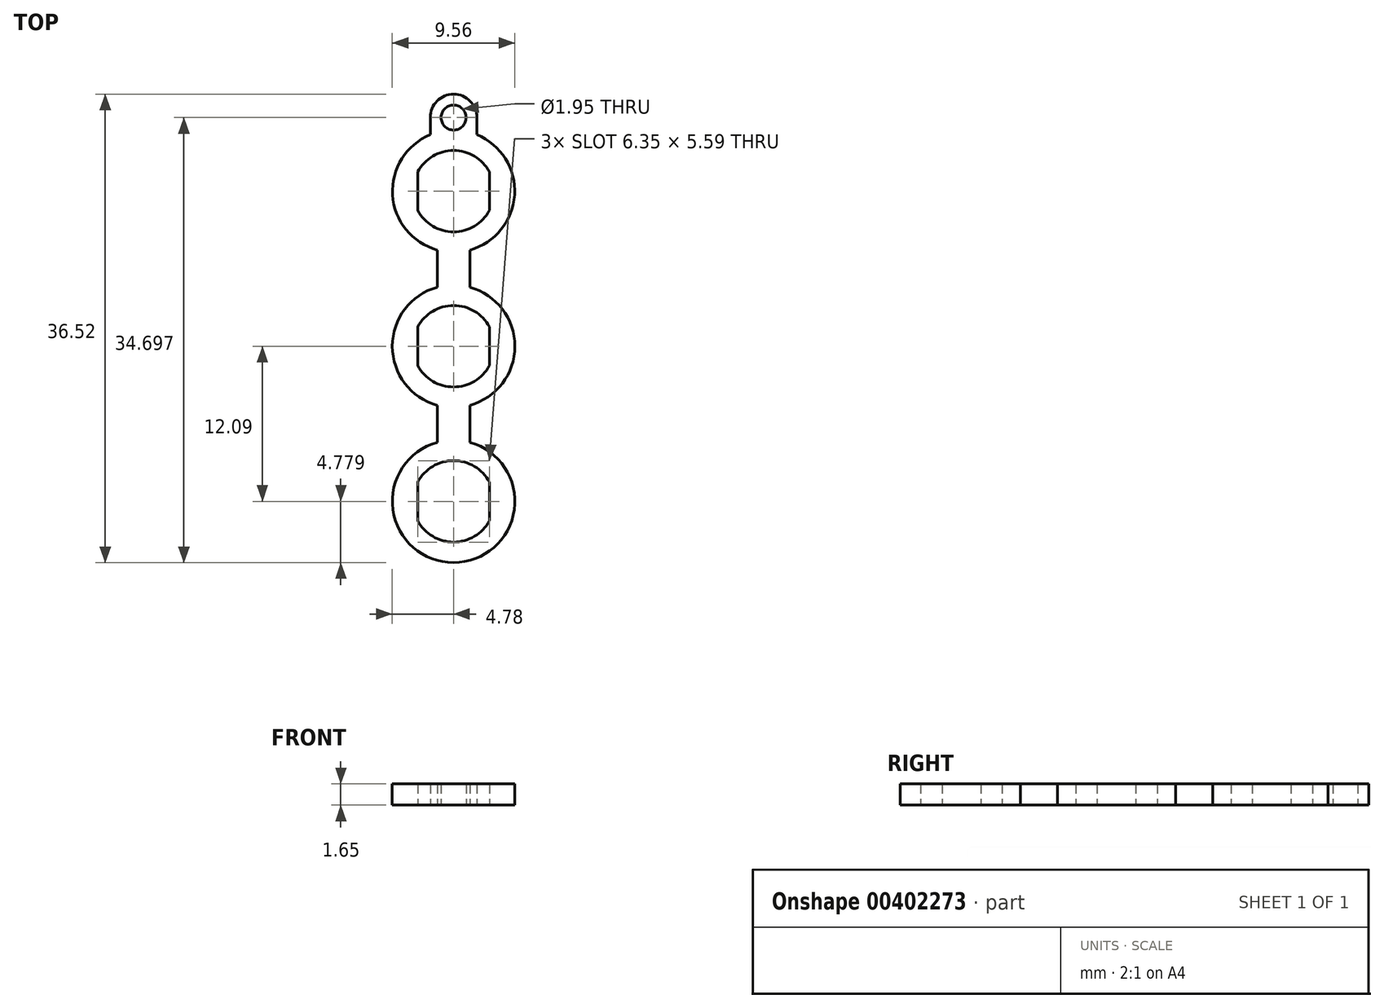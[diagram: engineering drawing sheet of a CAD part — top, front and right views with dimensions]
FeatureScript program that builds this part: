
annotation { "Feature Type Name" : "Feature", "Feature Type Description" : "" }
export const myFeature = defineFeature(function(context is Context, id is Id, definition is map)
    precondition{}
    {
        {
            var Q0;
            Q0=qCreatedBy(makeId("Top.planeOp"),FACE);
            var sketch = newSketch(context, id + "F0", { "sketchPlane" : qUnion([Q0])});
            skArc(sketch, "E0", {"start": v(1.27, -4.6) * mm, "mid": v(0, 4.76) * mm, "end": v(-1.27, -4.6) * mm});
            skArc(sketch, "E1", {"start": v(-1.27, -7.49) * mm, "mid": v(-4.78, -12.1) * mm, "end": v(-1.27, -16.7) * mm});
            skArc(sketch, "E2", {"start": v(-1.27, -19.58) * mm, "mid": v(0, -28.96) * mm, "end": v(1.27, -19.58) * mm});
            skLineSegment(sketch, "E3.0", {"start": v(-1.27, -4.6) * mm, "end": v(-1.27, -7.49) * mm});
            skLineSegment(sketch, "E4.0", {"start": v(1.27, -4.6) * mm, "end": v(1.27, -7.49) * mm});
            skLineSegment(sketch, "E5.trimOffspring", {"start": v(1.27, -16.7) * mm, "end": v(1.27, -19.58) * mm});
            skLineSegment(sketch, "E6.trimOffspring", {"start": v(-1.27, -16.7) * mm, "end": v(-1.27, -19.58) * mm});
            skArc(sketch, "E7", {"start": v(2.8, 1.5) * mm, "mid": v(0, 3.18) * mm, "end": v(-2.8, 1.5) * mm});
            skArc(sketch, "E8", {"start": v(2.8, -10.58) * mm, "mid": v(0, -8.92) * mm, "end": v(-2.8, -10.58) * mm});
            skArc(sketch, "E9", {"start": v(2.8, -22.67) * mm, "mid": v(0, -21) * mm, "end": v(-2.8, -22.67) * mm});
            skCircle(sketch, "E10", {"center": v(0, 5.74) * mm, "radius": 0.97 * mm});
            skArc(sketch, "E11", {"start": v(1.82, 5.74) * mm, "mid": v(0, 7.56) * mm, "end": v(-1.82, 5.74) * mm});
            skLineSegment(sketch, "E12", {"start": v(-1.82, 5.74) * mm, "end": v(-1.82, 4.4) * mm});
            skLineSegment(sketch, "E13", {"start": v(1.82, 5.74) * mm, "end": v(1.82, 4.4) * mm});
            skLineSegment(sketch, "E14.0", {"start": v(2.8, 1.5) * mm, "end": v(2.8, -1.5) * mm});
            skLineSegment(sketch, "E15.trimOffspring", {"start": v(-2.8, 1.5) * mm, "end": v(-2.8, -1.5) * mm});
            skArc(sketch, "E16.trimOffspring", {"start": v(-2.8, -1.5) * mm, "mid": v(0, -3.18) * mm, "end": v(2.8, -1.5) * mm});
            skLineSegment(sketch, "E17.trimOffspring", {"start": v(-2.8, -10.58) * mm, "end": v(-2.8, -13.6) * mm});
            skLineSegment(sketch, "E18.trimOffspring", {"start": v(2.8, -10.58) * mm, "end": v(2.8, -13.6) * mm});
            skLineSegment(sketch, "E19.trimOffspring", {"start": v(-2.8, -22.67) * mm, "end": v(-2.8, -25.69) * mm});
            skLineSegment(sketch, "E20.trimOffspring", {"start": v(2.8, -22.67) * mm, "end": v(2.8, -25.69) * mm});
            skArc(sketch, "E21.trimOffspring", {"start": v(-2.8, -13.6) * mm, "mid": v(0, -15.27) * mm, "end": v(2.8, -13.6) * mm});
            skArc(sketch, "E22.trimOffspring", {"start": v(-2.8, -25.69) * mm, "mid": v(0, -27.36) * mm, "end": v(2.8, -25.69) * mm});
            skArc(sketch, "E23.trimOffspring", {"start": v(1.27, -16.7) * mm, "mid": v(4.78, -12.1) * mm, "end": v(1.27, -7.49) * mm});
            skSolve(sketch);
        }
        {
            var Q0;
            {var subQ0=sQuery(id+"F0.wireOp",EDGE,"E10");Q0=makeQuery(id+"F0.imprint","IMPRINT",FACE,{"disambiguationData":[TD([[makeQuery(id+"F0.imprint","IMPRINT",EDGE,{"derivedFrom":subQ0}),-1.0]])]});}
            var Q1;
            Q1=makeQuery(id+"F0.imprint","IMPRINT",FACE,{"disambiguationData":[TD([[makeQuery(id+"F0.imprint","IMPRINT",EDGE,{"derivedFrom":sQuery(id+"F0.wireOp",EDGE,"E1")}),1.0]])]});
            extrude(context, id + "F1", {"entities" : qUnion([Q0, Q1]), "depth" : 1.65 * mm});
        }
    });
